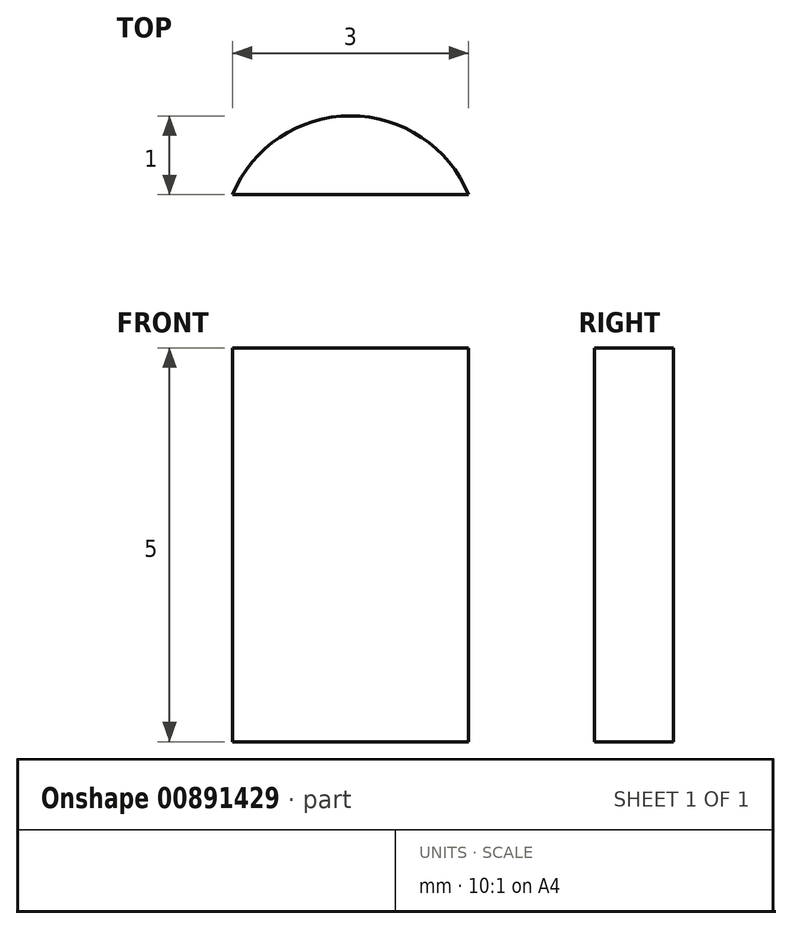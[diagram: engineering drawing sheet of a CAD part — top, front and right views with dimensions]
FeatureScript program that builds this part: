
annotation { "Feature Type Name" : "Feature", "Feature Type Description" : "" }
export const myFeature = defineFeature(function(context is Context, id is Id, definition is map)
    precondition{}
    {
        {
            var Q0;
            Q0=qCreatedBy(makeId("Top.planeOp"),FACE);
            var sketch = newSketch(context, id + "F0", { "sketchPlane" : qUnion([Q0])});
            skLineSegment(sketch, "E0", {"start": v(0, 0) * mm, "end": v(1.5, 0) * mm});
            skLineSegment(sketch, "E1", {"start": v(1.5, 0) * mm, "end": v(-1.5, 0) * mm});
            skLineSegment(sketch, "E2", {"start": v(0, 0) * mm, "end": v(0, 1) * mm});
            skArc(sketch, "E3", {"start": v(1.5, 0) * mm, "mid": v(0, 1) * mm, "end": v(-1.5, 0) * mm});
            skSolve(sketch);
        }
        {
            var Q0;
            {var subQ3=sQuery(id+"F0.wireOp",EDGE,"E2");Q0=makeQuery(id+"F0.imprint","IMPRINT",FACE,{"disambiguationData":[TD([[makeQuery(id+"F0.imprint","IMPRINT",EDGE,{"derivedFrom":subQ3}),-1.0]])]});}
            var Q1;
            {var subQ3=sQuery(id+"F0.wireOp",EDGE,"E2");Q1=makeQuery(id+"F0.imprint","IMPRINT",FACE,{"disambiguationData":[TD([[makeQuery(id+"F0.imprint","IMPRINT",EDGE,{"derivedFrom":subQ3}),1.0]])]});}
            extrude(context, id + "F1", {"entities" : qUnion([Q0, Q1]), "depth" : 5 * mm, "offsetDistance" : 25 * mm});
        }
    });
